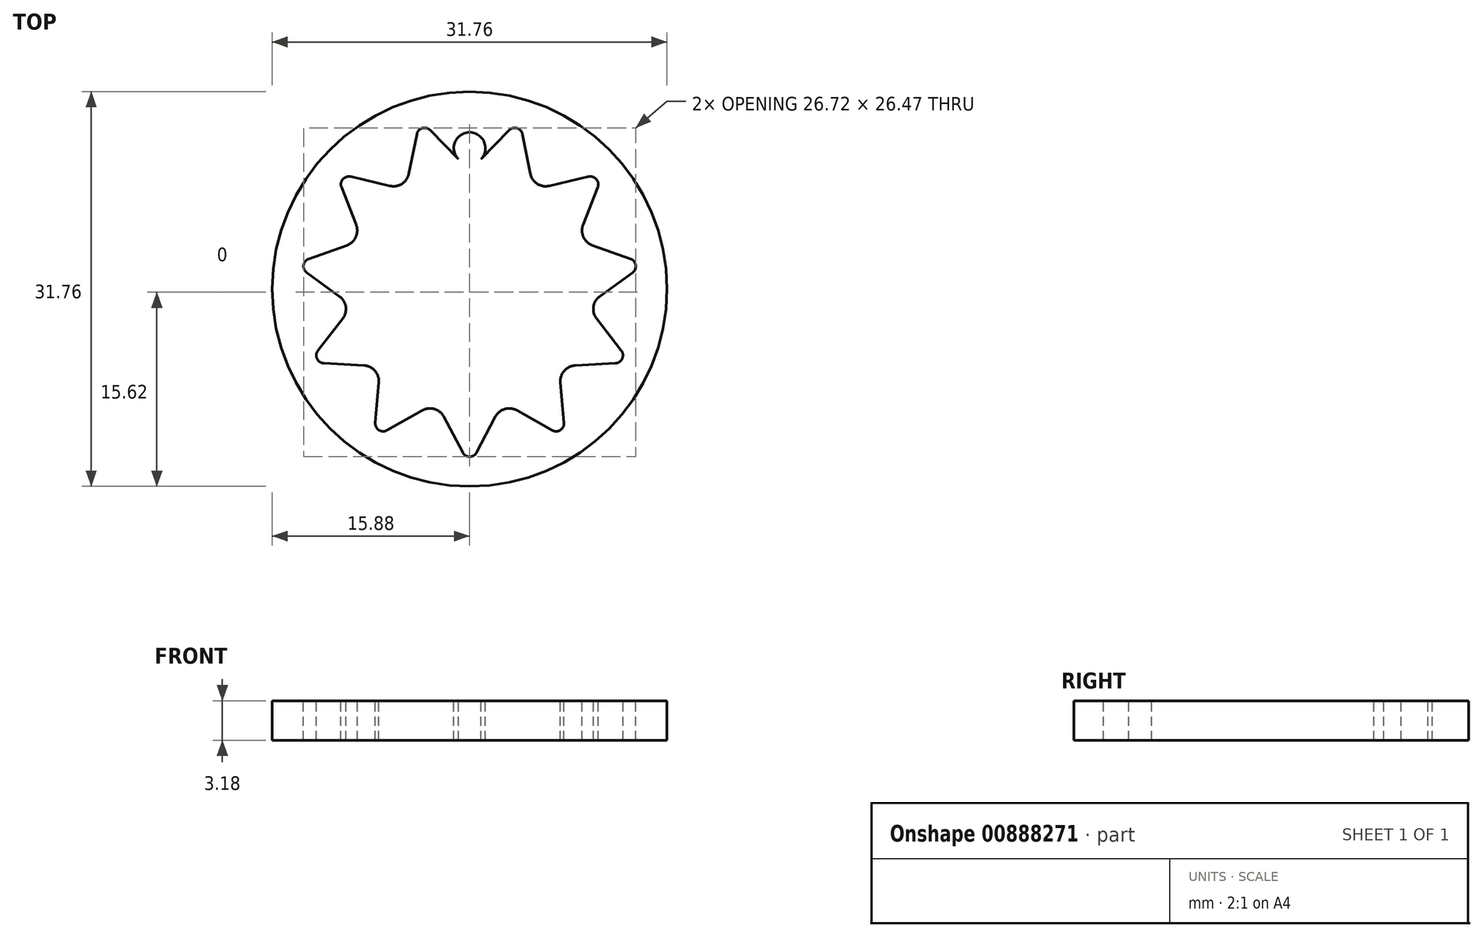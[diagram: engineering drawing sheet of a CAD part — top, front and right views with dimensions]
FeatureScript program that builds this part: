
annotation { "Feature Type Name" : "Feature", "Feature Type Description" : "" }
export const myFeature = defineFeature(function(context is Context, id is Id, definition is map)
    precondition{}
    {
        {
            var Q0;
            Q0=qCreatedBy(makeId("Top.planeOp"),FACE);
            var sketch = newSketch(context, id + "F0", { "sketchPlane" : qUnion([Q0])});
            skCircle(sketch, "E0", {"center": v(0, 0) * mm, "radius": 13.5 * mm});
            skLineSegment(sketch, "E1", {"start": v(0, 13.5) * mm, "end": v(0, 10.06) * mm});
            skCircle(sketch, "E2", {"center": v(0, 11.33) * mm, "radius": 1.27 * mm});
            skCircle(sketch, "E3.1.0", {"center": v(-6.13, 9.54) * mm, "radius": 1.27 * mm});
            skCircle(sketch, "E3.2.0", {"center": v(-10.31, 4.7) * mm, "radius": 1.27 * mm});
            skCircle(sketch, "E3.3.0", {"center": v(-11.22, -1.61) * mm, "radius": 1.27 * mm});
            skCircle(sketch, "E3.4.0", {"center": v(-8.57, -7.42) * mm, "radius": 1.27 * mm});
            skCircle(sketch, "E3.5.0", {"center": v(-3.2, -10.88) * mm, "radius": 1.27 * mm});
            skCircle(sketch, "E3.6.0", {"center": v(3.2, -10.88) * mm, "radius": 1.27 * mm});
            skCircle(sketch, "E3.7.0", {"center": v(8.57, -7.42) * mm, "radius": 1.27 * mm});
            skCircle(sketch, "E3.8.0", {"center": v(11.22, -1.61) * mm, "radius": 1.27 * mm});
            skCircle(sketch, "E3.9.0", {"center": v(10.31, 4.7) * mm, "radius": 1.27 * mm});
            skCircle(sketch, "E3.10.0", {"center": v(6.13, 9.54) * mm, "radius": 1.27 * mm});
            skLineSegment(sketch, "E4", {"start": v(0, 0) * mm, "end": v(3.8, 12.95) * mm});
            skCircle(sketch, "E5", {"center": v(3.62, 12.34) * mm, "radius": 0.64 * mm});
            skCircle(sketch, "E6.1.0", {"center": v(-3.62, 12.34) * mm, "radius": 0.64 * mm});
            skCircle(sketch, "E6.2.0", {"center": v(-9.72, 8.42) * mm, "radius": 0.64 * mm});
            skCircle(sketch, "E7.1.3.0", {"center": v(-12.73, 1.83) * mm, "radius": 0.64 * mm});
            skCircle(sketch, "E7.1.4.0", {"center": v(-11.7, -5.34) * mm, "radius": 0.64 * mm});
            skCircle(sketch, "E7.1.5.0", {"center": v(-6.95, -10.82) * mm, "radius": 0.64 * mm});
            skCircle(sketch, "E7.1.6.0", {"center": v(0, -12.86) * mm, "radius": 0.64 * mm});
            skCircle(sketch, "E7.1.7.0", {"center": v(6.95, -10.82) * mm, "radius": 0.64 * mm});
            skCircle(sketch, "E7.1.8.0", {"center": v(11.7, -5.34) * mm, "radius": 0.64 * mm});
            skCircle(sketch, "E7.1.9.0", {"center": v(12.73, 1.83) * mm, "radius": 0.64 * mm});
            skCircle(sketch, "E7.1.10.0", {"center": v(9.72, 8.42) * mm, "radius": 0.64 * mm});
            skLineSegment(sketch, "E8", {"start": v(-9.13, 5.17) * mm, "end": v(-10.3, 8.19) * mm});
            skLineSegment(sketch, "E9", {"start": v(-9.89, 3.51) * mm, "end": v(-12.94, 2.43) * mm});
            skLineSegment(sketch, "E10", {"start": v(-9.57, 9.04) * mm, "end": v(-6.42, 8.3) * mm});
            skLineSegment(sketch, "E11", {"start": v(-13.1, 1.32) * mm, "end": v(-10.47, -0.58) * mm});
            skLineSegment(sketch, "E12", {"start": v(-10.22, -2.4) * mm, "end": v(-12.2, -4.95) * mm});
            skLineSegment(sketch, "E13", {"start": v(-7.3, -7.53) * mm, "end": v(-7.58, -10.76) * mm});
            skLineSegment(sketch, "E14", {"start": v(-6.64, -11.37) * mm, "end": v(-3.82, -9.77) * mm});
            skLineSegment(sketch, "E15", {"start": v(-2.07, -10.29) * mm, "end": v(-0.56, -13.15) * mm});
            skLineSegment(sketch, "E16", {"start": v(0.56, -13.15) * mm, "end": v(2.07, -10.29) * mm});
            skLineSegment(sketch, "E17", {"start": v(3.82, -9.77) * mm, "end": v(6.64, -11.37) * mm});
            skLineSegment(sketch, "E18", {"start": v(7.58, -10.76) * mm, "end": v(7.3, -7.53) * mm});
            skLineSegment(sketch, "E19", {"start": v(8.5, -6.15) * mm, "end": v(11.73, -5.98) * mm});
            skLineSegment(sketch, "E20", {"start": v(-4.88, 9.29) * mm, "end": v(-4.25, 12.46) * mm});
            skLineSegment(sketch, "E21", {"start": v(-3.17, 12.78) * mm, "end": v(-0.91, 10.45) * mm});
            skLineSegment(sketch, "E22", {"start": v(0.91, 10.45) * mm, "end": v(3.17, 12.78) * mm});
            skLineSegment(sketch, "E23", {"start": v(10.3, 8.19) * mm, "end": v(9.13, 5.17) * mm});
            skLineSegment(sketch, "E24", {"start": v(9.89, 3.51) * mm, "end": v(12.94, 2.43) * mm});
            skLineSegment(sketch, "E25", {"start": v(13.1, 1.32) * mm, "end": v(10.47, -0.58) * mm});
            skLineSegment(sketch, "E26", {"start": v(10.22, -2.4) * mm, "end": v(12.2, -4.95) * mm});
            skLineSegment(sketch, "E27", {"start": v(4.25, 12.46) * mm, "end": v(4.88, 9.29) * mm});
            skLineSegment(sketch, "E28", {"start": v(6.42, 8.3) * mm, "end": v(9.57, 9.04) * mm});
            skLineSegment(sketch, "E29", {"start": v(-11.73, -5.98) * mm, "end": v(-8.5, -6.15) * mm});
            skCircle(sketch, "E30", {"center": v(0, 0) * mm, "radius": 15.88 * mm});
            skSolve(sketch);
        }
        {
            var Q0;
            Q0=makeQuery(id+"F0.imprint","IMPRINT",FACE,{"disambiguationData":[TD([[makeQuery(id+"F0.imprint","IMPRINT",EDGE,{"derivedFrom":sQuery(id+"F0.wireOp",EDGE,"E30")}),1.0]])]});
            var Q1;
            {var subQ0=sQuery(id+"F0.wireOp",EDGE,"E10");Q1=makeQuery(id+"F0.imprint","IMPRINT",FACE,{"disambiguationData":[TD([[makeQuery(id+"F0.imprint","IMPRINT",EDGE,{"derivedFrom":subQ0}),1.0]])]});}
            var Q2;
            {var subQ0=sQuery(id+"F0.wireOp",EDGE,"E3.1.0");var subQ1=makeQuery(id+"F0.imprint","INTERSECT",VERTEX,{"derivedFrom":[subQ0,sQuery(id+"F0.wireOp",EDGE,"E10")]});Q2=makeQuery(id+"F0.imprint","IMPRINT",FACE,{"disambiguationData":[TD([[makeQuery(id+"F0.imprint","IMPRINT",EDGE,{"disambiguationData":[TD([[subQ1,-1.0]])],"derivedFrom":subQ0}),1.0]])]});}
            var Q3;
            {var subQ4=sQuery(id+"F0.wireOp",EDGE,"E11");Q3=makeQuery(id+"F0.imprint","IMPRINT",FACE,{"disambiguationData":[TD([[makeQuery(id+"F0.imprint","IMPRINT",EDGE,{"derivedFrom":subQ4}),-1.0]])]});}
            var Q4;
            {var subQ0=sQuery(id+"F0.wireOp",EDGE,"E3.3.0");var subQ1=makeQuery(id+"F0.imprint","INTERSECT",VERTEX,{"derivedFrom":[subQ0,sQuery(id+"F0.wireOp",EDGE,"E11")]});Q4=makeQuery(id+"F0.imprint","IMPRINT",FACE,{"disambiguationData":[TD([[makeQuery(id+"F0.imprint","IMPRINT",EDGE,{"disambiguationData":[TD([[subQ1,1.0]])],"derivedFrom":subQ0}),1.0]])]});}
            var Q5;
            {var subQ6=sQuery(id+"F0.wireOp",EDGE,"E8");Q5=makeQuery(id+"F0.imprint","IMPRINT",FACE,{"disambiguationData":[TD([[makeQuery(id+"F0.imprint","IMPRINT",EDGE,{"derivedFrom":subQ6}),1.0]])]});}
            var Q6;
            {var subQ0=sQuery(id+"F0.wireOp",EDGE,"E3.2.0");var subQ1=makeQuery(id+"F0.imprint","INTERSECT",VERTEX,{"derivedFrom":[subQ0,sQuery(id+"F0.wireOp",EDGE,"E8")]});Q6=makeQuery(id+"F0.imprint","IMPRINT",FACE,{"disambiguationData":[TD([[makeQuery(id+"F0.imprint","IMPRINT",EDGE,{"disambiguationData":[TD([[subQ1,1.0]])],"derivedFrom":subQ0}),1.0]])]});}
            var Q7;
            {var subQ0=sQuery(id+"F0.wireOp",EDGE,"E21");Q7=makeQuery(id+"F0.imprint","IMPRINT",FACE,{"disambiguationData":[TD([[makeQuery(id+"F0.imprint","IMPRINT",EDGE,{"derivedFrom":subQ0}),1.0]])]});}
            var Q8;
            {var subQ0=sQuery(id+"F0.wireOp",EDGE,"E2");var subQ1=sQuery(id+"F0.wireOp",EDGE,"E1");var subQ2=makeQuery(id+"F0.imprint","INTERSECT",VERTEX,{"disambiguationData":[OD(0.0)],"derivedFrom":[subQ1,subQ0]});Q8=makeQuery(id+"F0.imprint","IMPRINT",FACE,{"disambiguationData":[TD([[makeQuery(id+"F0.imprint","IMPRINT",EDGE,{"disambiguationData":[TD([[subQ2,1.0]])],"derivedFrom":subQ1}),1.0]])]});}
            var Q9;
            {var subQ3=sQuery(id+"F0.wireOp",EDGE,"E22");Q9=makeQuery(id+"F0.imprint","IMPRINT",FACE,{"disambiguationData":[TD([[makeQuery(id+"F0.imprint","IMPRINT",EDGE,{"derivedFrom":subQ3}),1.0]])]});}
            var Q10;
            {var subQ0=sQuery(id+"F0.wireOp",EDGE,"E2");var subQ1=sQuery(id+"F0.wireOp",EDGE,"E1");var subQ2=makeQuery(id+"F0.imprint","INTERSECT",VERTEX,{"disambiguationData":[OD(0.0)],"derivedFrom":[subQ1,subQ0]});Q10=makeQuery(id+"F0.imprint","IMPRINT",FACE,{"disambiguationData":[TD([[makeQuery(id+"F0.imprint","IMPRINT",EDGE,{"disambiguationData":[TD([[subQ2,1.0]])],"derivedFrom":subQ1}),-1.0]])]});}
            var Q11;
            {var subQ3=sQuery(id+"F0.wireOp",EDGE,"E27");Q11=makeQuery(id+"F0.imprint","IMPRINT",FACE,{"disambiguationData":[TD([[makeQuery(id+"F0.imprint","IMPRINT",EDGE,{"derivedFrom":subQ3}),1.0]])]});}
            var Q12;
            {var subQ0=sQuery(id+"F0.wireOp",EDGE,"E3.10.0");var subQ1=makeQuery(id+"F0.imprint","INTERSECT",VERTEX,{"derivedFrom":[subQ0,sQuery(id+"F0.wireOp",EDGE,"E27")]});Q12=makeQuery(id+"F0.imprint","IMPRINT",FACE,{"disambiguationData":[TD([[makeQuery(id+"F0.imprint","IMPRINT",EDGE,{"disambiguationData":[TD([[subQ1,-1.0]])],"derivedFrom":subQ0}),1.0]])]});}
            var Q13;
            {var subQ4=sQuery(id+"F0.wireOp",EDGE,"E23");Q13=makeQuery(id+"F0.imprint","IMPRINT",FACE,{"disambiguationData":[TD([[makeQuery(id+"F0.imprint","IMPRINT",EDGE,{"derivedFrom":subQ4}),1.0]])]});}
            var Q14;
            {var subQ0=sQuery(id+"F0.wireOp",EDGE,"E3.9.0");var subQ1=makeQuery(id+"F0.imprint","INTERSECT",VERTEX,{"derivedFrom":[subQ0,sQuery(id+"F0.wireOp",EDGE,"E23")]});Q14=makeQuery(id+"F0.imprint","IMPRINT",FACE,{"disambiguationData":[TD([[makeQuery(id+"F0.imprint","IMPRINT",EDGE,{"disambiguationData":[TD([[subQ1,-1.0]])],"derivedFrom":subQ0}),1.0]])]});}
            var Q15;
            {var subQ0=sQuery(id+"F0.wireOp",EDGE,"E25");Q15=makeQuery(id+"F0.imprint","IMPRINT",FACE,{"disambiguationData":[TD([[makeQuery(id+"F0.imprint","IMPRINT",EDGE,{"derivedFrom":subQ0}),1.0]])]});}
            var Q16;
            {var subQ0=sQuery(id+"F0.wireOp",EDGE,"E3.8.0");var subQ1=makeQuery(id+"F0.imprint","INTERSECT",VERTEX,{"derivedFrom":[subQ0,sQuery(id+"F0.wireOp",EDGE,"E25")]});Q16=makeQuery(id+"F0.imprint","IMPRINT",FACE,{"disambiguationData":[TD([[makeQuery(id+"F0.imprint","IMPRINT",EDGE,{"disambiguationData":[TD([[subQ1,-1.0]])],"derivedFrom":subQ0}),1.0]])]});}
            var Q17;
            {var subQ4=sQuery(id+"F0.wireOp",EDGE,"E18");Q17=makeQuery(id+"F0.imprint","IMPRINT",FACE,{"disambiguationData":[TD([[makeQuery(id+"F0.imprint","IMPRINT",EDGE,{"derivedFrom":subQ4}),-1.0]])]});}
            var Q18;
            {var subQ0=sQuery(id+"F0.wireOp",EDGE,"E3.7.0");var subQ1=makeQuery(id+"F0.imprint","INTERSECT",VERTEX,{"derivedFrom":[subQ0,sQuery(id+"F0.wireOp",EDGE,"E18")]});Q18=makeQuery(id+"F0.imprint","IMPRINT",FACE,{"disambiguationData":[TD([[makeQuery(id+"F0.imprint","IMPRINT",EDGE,{"disambiguationData":[TD([[subQ1,1.0]])],"derivedFrom":subQ0}),1.0]])]});}
            var Q19;
            {var subQ4=sQuery(id+"F0.wireOp",EDGE,"E16");Q19=makeQuery(id+"F0.imprint","IMPRINT",FACE,{"disambiguationData":[TD([[makeQuery(id+"F0.imprint","IMPRINT",EDGE,{"derivedFrom":subQ4}),-1.0]])]});}
            var Q20;
            {var subQ0=sQuery(id+"F0.wireOp",EDGE,"E3.6.0");var subQ1=makeQuery(id+"F0.imprint","INTERSECT",VERTEX,{"derivedFrom":[subQ0,sQuery(id+"F0.wireOp",EDGE,"E16")]});Q20=makeQuery(id+"F0.imprint","IMPRINT",FACE,{"disambiguationData":[TD([[makeQuery(id+"F0.imprint","IMPRINT",EDGE,{"disambiguationData":[TD([[subQ1,1.0]])],"derivedFrom":subQ0}),1.0]])]});}
            var Q21;
            {var subQ0=sQuery(id+"F0.wireOp",EDGE,"E14");Q21=makeQuery(id+"F0.imprint","IMPRINT",FACE,{"disambiguationData":[TD([[makeQuery(id+"F0.imprint","IMPRINT",EDGE,{"derivedFrom":subQ0}),-1.0]])]});}
            var Q22;
            {var subQ0=sQuery(id+"F0.wireOp",EDGE,"E3.5.0");var subQ1=makeQuery(id+"F0.imprint","INTERSECT",VERTEX,{"derivedFrom":[subQ0,sQuery(id+"F0.wireOp",EDGE,"E14")]});Q22=makeQuery(id+"F0.imprint","IMPRINT",FACE,{"disambiguationData":[TD([[makeQuery(id+"F0.imprint","IMPRINT",EDGE,{"disambiguationData":[TD([[subQ1,1.0]])],"derivedFrom":subQ0}),1.0]])]});}
            var Q23;
            {var subQ4=sQuery(id+"F0.wireOp",EDGE,"E13");Q23=makeQuery(id+"F0.imprint","IMPRINT",FACE,{"disambiguationData":[TD([[makeQuery(id+"F0.imprint","IMPRINT",EDGE,{"derivedFrom":subQ4}),-1.0]])]});}
            var Q24;
            {var subQ0=sQuery(id+"F0.wireOp",EDGE,"E3.4.0");var subQ1=makeQuery(id+"F0.imprint","INTERSECT",VERTEX,{"derivedFrom":[subQ0,sQuery(id+"F0.wireOp",EDGE,"E13")]});Q24=makeQuery(id+"F0.imprint","IMPRINT",FACE,{"disambiguationData":[TD([[makeQuery(id+"F0.imprint","IMPRINT",EDGE,{"disambiguationData":[TD([[subQ1,-1.0]])],"derivedFrom":subQ0}),1.0]])]});}
            extrude(context, id + "F1", {"entities" : qUnion([Q0, Q1, Q2, Q3, Q4, Q5, Q6, Q7, Q8, Q9, Q10, Q11, Q12, Q13, Q14, Q15, Q16, Q17, Q18, Q19, Q20, Q21, Q22, Q23, Q24]), "oppositeDirection" : true, "depth" : 3.17 * mm, "offsetDistance" : 25.4 * mm});
        }
    });
